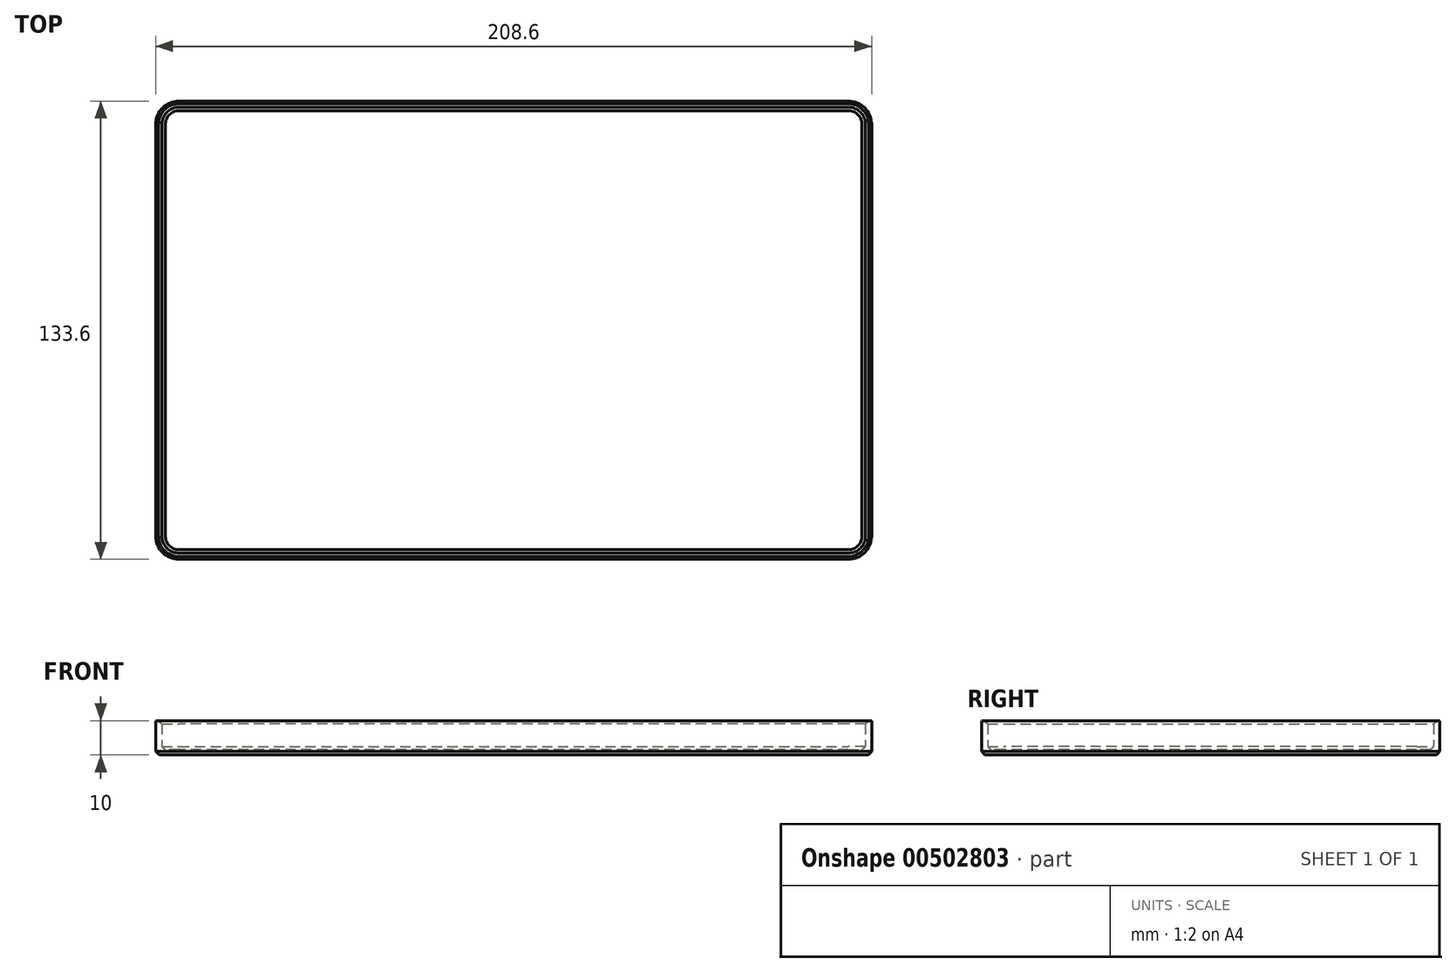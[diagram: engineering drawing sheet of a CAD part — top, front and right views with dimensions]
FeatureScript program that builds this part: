
annotation { "Feature Type Name" : "Feature", "Feature Type Description" : "" }
export const myFeature = defineFeature(function(context is Context, id is Id, definition is map)
    precondition{}
    {
        {
            var Q0;
            Q0=qCreatedBy(makeId("Top.planeOp"),FACE);
            var sketch = newSketch(context, id + "F0", { "sketchPlane" : qUnion([Q0])});
            skLineSegment(sketch, "E0.bottom", {"start": v(97.5, 65) * mm, "end": v(-97.5, 65) * mm});
            skLineSegment(sketch, "E0.top", {"start": v(97.5, -65) * mm, "end": v(-97.5, -65) * mm});
            skLineSegment(sketch, "E0.left", {"start": v(102.5, 60) * mm, "end": v(102.5, -60) * mm});
            skLineSegment(sketch, "E0.right", {"start": v(-102.5, 60) * mm, "end": v(-102.5, -60) * mm});
            skPoint(sketch, "E0.middle", {"position": v(0, 0) * mm});
            skPoint(sketch, "E1.visualSharp", {"position": v(-102.5, 65) * mm});
            skArc(sketch, "E1.filletArc", {"start": v(-97.5, 65) * mm, "mid": v(-101.04, 63.54) * mm, "end": v(-102.5, 60) * mm});
            skPoint(sketch, "E2.visualSharp", {"position": v(102.5, 65) * mm});
            skArc(sketch, "E2.filletArc", {"start": v(102.5, 60) * mm, "mid": v(101.04, 63.54) * mm, "end": v(97.5, 65) * mm});
            skPoint(sketch, "E3.visualSharp", {"position": v(102.5, -65) * mm});
            skArc(sketch, "E3.filletArc", {"start": v(97.5, -65) * mm, "mid": v(101.04, -63.54) * mm, "end": v(102.5, -60) * mm});
            skPoint(sketch, "E4.visualSharp", {"position": v(-102.5, -65) * mm});
            skArc(sketch, "E4.filletArc", {"start": v(-102.5, -60) * mm, "mid": v(-101.04, -63.54) * mm, "end": v(-97.5, -65) * mm});
            skArc(sketch, "E5.0", {"start": v(104.3, 60) * mm, "mid": v(102.3, 64.8) * mm, "end": v(97.5, 66.8) * mm});
            skLineSegment(sketch, "E5.1", {"start": v(104.3, 60) * mm, "end": v(104.3, -60) * mm});
            skLineSegment(sketch, "E5.2", {"start": v(97.5, 66.8) * mm, "end": v(-97.5, 66.8) * mm});
            skArc(sketch, "E5.3", {"start": v(97.5, -66.8) * mm, "mid": v(102.3, -64.8) * mm, "end": v(104.3, -60) * mm});
            skArc(sketch, "E5.4", {"start": v(-97.5, 66.8) * mm, "mid": v(-102.3, 64.8) * mm, "end": v(-104.3, 60) * mm});
            skLineSegment(sketch, "E5.5", {"start": v(-104.3, 60) * mm, "end": v(-104.3, -60) * mm});
            skArc(sketch, "E5.6", {"start": v(-104.3, -60) * mm, "mid": v(-102.3, -64.8) * mm, "end": v(-97.5, -66.8) * mm});
            skLineSegment(sketch, "E5.7", {"start": v(97.5, -66.8) * mm, "end": v(-97.5, -66.8) * mm});
            skSolve(sketch);
        }
        {
            var Q0;
            Q0=makeQuery(id+"F0.imprint","IMPRINT",FACE,{"disambiguationData":[TD([[makeQuery(id+"F0.imprint","IMPRINT",EDGE,{"derivedFrom":sQuery(id+"F0.wireOp",EDGE,"E0.bottom")}),1.0]])]});
            extrude(context, id + "F1", {"entities" : qUnion([Q0]), "depth" : 1.5 * mm, "offsetDistance" : 25 * mm});
        }
        {
            var Q0;
            Q0=makeQuery(id+"F0.imprint","IMPRINT",FACE,{"disambiguationData":[TD([[makeQuery(id+"F0.imprint","IMPRINT",EDGE,{"derivedFrom":sQuery(id+"F0.wireOp",EDGE,"E0.bottom")}),-1.0]])]});
            extrude(context, id + "F2", {"entities" : qUnion([Q0]), "operationType" : NewBodyOperationType.ADD, "depth" : 10 * mm, "offsetDistance" : 25 * mm});
        }
        {
            var Q0;
            {var subQ0=sQuery(id+"F0.wireOp",EDGE,"E4.filletArc");var subQ1=sQuery(id+"F0.wireOp",EDGE,"E3.filletArc");var subQ2=sQuery(id+"F0.wireOp",EDGE,"E2.filletArc");var subQ3=sQuery(id+"F0.wireOp",EDGE,"E1.filletArc");var subQ4=sQuery(id+"F0.wireOp",EDGE,"E0.right");var subQ5=sQuery(id+"F0.wireOp",EDGE,"E0.left");var subQ6=sQuery(id+"F0.wireOp",EDGE,"E0.top");var subQ7=sQuery(id+"F0.wireOp",EDGE,"E0.bottom");Q0=makeQuery(id+"F2.boolean.opBoolean","MERGE",FACE,{"derivedFrom":[makeQuery(id+"F1.opExtrude","CAP_FACE",FACE,{"disambiguationData":[OSD([subQ7,subQ6,subQ5,subQ4,subQ3,subQ2,subQ1,subQ0])],"isStart":true}),makeQuery(id+"F2.opExtrude","CAP_FACE",FACE,{"disambiguationData":[OSD([subQ7,subQ6,subQ5,subQ4,subQ3,subQ2,subQ1,subQ0,sQuery(id+"F0.wireOp",EDGE,"E5.0"),sQuery(id+"F0.wireOp",EDGE,"E5.1"),sQuery(id+"F0.wireOp",EDGE,"E5.2"),sQuery(id+"F0.wireOp",EDGE,"E5.3"),sQuery(id+"F0.wireOp",EDGE,"E5.4"),sQuery(id+"F0.wireOp",EDGE,"E5.5"),sQuery(id+"F0.wireOp",EDGE,"E5.6"),sQuery(id+"F0.wireOp",EDGE,"E5.7")])],"isStart":true})]});}
            var Q1;
            Q1=makeQuery(id+"F1.opExtrude","CAP_FACE",FACE,{"disambiguationData":[OSD([sQuery(id+"F0.wireOp",EDGE,"E0.bottom"),sQuery(id+"F0.wireOp",EDGE,"E0.top"),sQuery(id+"F0.wireOp",EDGE,"E0.left"),sQuery(id+"F0.wireOp",EDGE,"E0.right"),sQuery(id+"F0.wireOp",EDGE,"E1.filletArc"),sQuery(id+"F0.wireOp",EDGE,"E2.filletArc"),sQuery(id+"F0.wireOp",EDGE,"E3.filletArc"),sQuery(id+"F0.wireOp",EDGE,"E4.filletArc")])],"isStart":false});
            var Q2;
            Q2=makeQuery(id+"F2.opExtrude","SWEPT_FACE",FACE,{"disambiguationData":[OSD([sQuery(id+"F0.wireOp",EDGE,"E0.bottom")])]});
            chamfer(context, id + "F3", {"entities" : qUnion([Q0, Q1, Q2]), "width" : 1 * mm, "tangentPropagation" : true});
        }
    });
